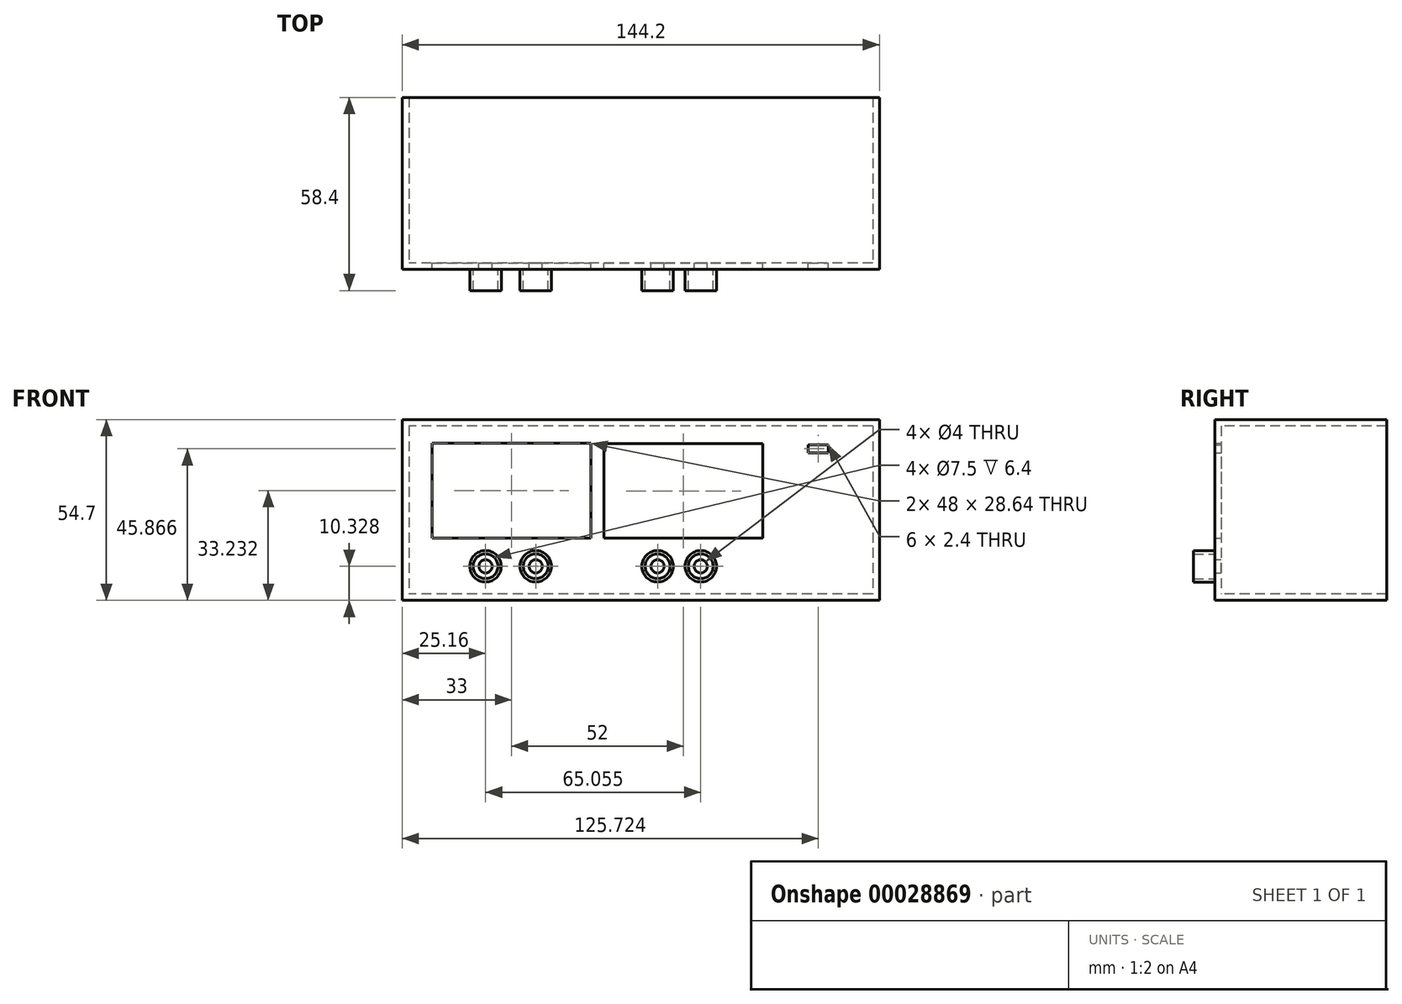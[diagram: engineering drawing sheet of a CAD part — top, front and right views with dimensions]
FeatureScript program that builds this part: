
annotation { "Feature Type Name" : "Feature", "Feature Type Description" : "" }
export const myFeature = defineFeature(function(context is Context, id is Id, definition is map)
    precondition{}
    {
        {
            var Q0;
            Q0=qCreatedBy(makeId("Front.planeOp"),FACE);
            var sketch = newSketch(context, id + "F0", { "sketchPlane" : qUnion([Q0])});
            skLineSegment(sketch, "E0.bottom", {"start": v(0, 54.7) * mm, "end": v(144.2, 54.7) * mm});
            skLineSegment(sketch, "E0.top", {"start": v(0, 0) * mm, "end": v(144.2, 0) * mm});
            skLineSegment(sketch, "E0.left", {"start": v(0, 54.7) * mm, "end": v(0, 0) * mm});
            skLineSegment(sketch, "E0.right", {"start": v(144.2, 54.7) * mm, "end": v(144.2, 0) * mm});
            skLineSegment(sketch, "E1.bottom", {"start": v(9, 47.55) * mm, "end": v(57, 47.55) * mm});
            skLineSegment(sketch, "E1.top", {"start": v(9, 18.91) * mm, "end": v(57, 18.91) * mm});
            skLineSegment(sketch, "E1.left", {"start": v(9, 47.55) * mm, "end": v(9, 18.91) * mm});
            skLineSegment(sketch, "E1.right", {"start": v(57, 47.55) * mm, "end": v(57, 18.91) * mm});
            skLineSegment(sketch, "E2.bottom", {"start": v(61, 47.46) * mm, "end": v(109, 47.46) * mm});
            skLineSegment(sketch, "E2.top", {"start": v(61, 18.82) * mm, "end": v(109, 18.82) * mm});
            skLineSegment(sketch, "E2.left", {"start": v(61, 47.46) * mm, "end": v(61, 18.82) * mm});
            skLineSegment(sketch, "E2.right", {"start": v(109, 47.46) * mm, "end": v(109, 18.82) * mm});
            skLineSegment(sketch, "E3.bottom", {"start": v(122.72, 47.07) * mm, "end": v(128.72, 47.07) * mm});
            skLineSegment(sketch, "E3.top", {"start": v(122.72, 44.67) * mm, "end": v(128.72, 44.67) * mm});
            skLineSegment(sketch, "E3.left", {"start": v(122.72, 47.07) * mm, "end": v(122.72, 44.67) * mm});
            skLineSegment(sketch, "E3.right", {"start": v(128.72, 47.07) * mm, "end": v(128.72, 44.67) * mm});
            skLineSegment(sketch, "E4", {"start": v(0, 10.33) * mm, "end": v(144.2, 10.33) * mm, "construction": true});
            skCircle(sketch, "E5", {"center": v(25.16, 10.33) * mm, "radius": 2 * mm});
            skCircle(sketch, "E6", {"center": v(40.32, 10.33) * mm, "radius": 2 * mm});
            skCircle(sketch, "E7", {"center": v(77.16, 10.33) * mm, "radius": 2 * mm});
            skCircle(sketch, "E8", {"center": v(90.22, 10.33) * mm, "radius": 2 * mm});
            skSolve(sketch);
        }
        {
            var Q0;
            Q0=makeQuery(id+"F0.imprint","IMPRINT",FACE,{"disambiguationData":[TD([[makeQuery(id+"F0.imprint","IMPRINT",EDGE,{"derivedFrom":sQuery(id+"F0.wireOp",EDGE,"E0.bottom")}),-1.0]])]});
            extrude(context, id + "F1", {"entities" : qUnion([Q0]), "depth" : 2 * mm});
        }
        {
            var Q0;
            Q0=makeQuery(id+"F1.opExtrude","CAP_FACE",FACE,{"disambiguationData":[OSD([sQuery(id+"F0.wireOp",EDGE,"E0.bottom"),sQuery(id+"F0.wireOp",EDGE,"E0.top"),sQuery(id+"F0.wireOp",EDGE,"E0.left"),sQuery(id+"F0.wireOp",EDGE,"E0.right"),sQuery(id+"F0.wireOp",EDGE,"E1.bottom"),sQuery(id+"F0.wireOp",EDGE,"E1.top"),sQuery(id+"F0.wireOp",EDGE,"E1.left"),sQuery(id+"F0.wireOp",EDGE,"E1.right"),sQuery(id+"F0.wireOp",EDGE,"E2.bottom"),sQuery(id+"F0.wireOp",EDGE,"E2.top"),sQuery(id+"F0.wireOp",EDGE,"E2.left"),sQuery(id+"F0.wireOp",EDGE,"E2.right"),sQuery(id+"F0.wireOp",EDGE,"E3.bottom"),sQuery(id+"F0.wireOp",EDGE,"E3.top"),sQuery(id+"F0.wireOp",EDGE,"E3.left"),sQuery(id+"F0.wireOp",EDGE,"E3.right"),sQuery(id+"F0.wireOp",EDGE,"E5"),sQuery(id+"F0.wireOp",EDGE,"E6"),sQuery(id+"F0.wireOp",EDGE,"E7"),sQuery(id+"F0.wireOp",EDGE,"E8")])],"isStart":false});
            var sketch = newSketch(context, id + "F2", { "sketchPlane" : qUnion([Q0])});
            skCircle(sketch, "E9", {"center": v(25.16, 10.33) * mm, "radius": 4.75 * mm});
            skCircle(sketch, "E10", {"center": v(40.32, 10.33) * mm, "radius": 4.75 * mm});
            skCircle(sketch, "E11", {"center": v(77.16, 10.33) * mm, "radius": 4.75 * mm});
            skCircle(sketch, "E12", {"center": v(90.22, 10.33) * mm, "radius": 4.75 * mm});
            skCircle(sketch, "E13", {"center": v(25.16, 10.33) * mm, "radius": 3.75 * mm});
            skCircle(sketch, "E14", {"center": v(40.32, 10.33) * mm, "radius": 3.75 * mm});
            skCircle(sketch, "E15", {"center": v(77.16, 10.33) * mm, "radius": 3.75 * mm});
            skCircle(sketch, "E16", {"center": v(90.22, 10.33) * mm, "radius": 3.75 * mm});
            skSolve(sketch);
        }
        {
            var Q0;
            Q0=makeQuery(id+"F2.imprint","IMPRINT",FACE,{"disambiguationData":[TD([[makeQuery(id+"F2.imprint","IMPRINT",EDGE,{"derivedFrom":sQuery(id+"F2.wireOp",EDGE,"E9")}),1.0]])]});
            var Q1;
            Q1=makeQuery(id+"F2.imprint","IMPRINT",FACE,{"disambiguationData":[TD([[makeQuery(id+"F2.imprint","IMPRINT",EDGE,{"derivedFrom":sQuery(id+"F2.wireOp",EDGE,"E10")}),1.0]])]});
            var Q2;
            Q2=makeQuery(id+"F2.imprint","IMPRINT",FACE,{"disambiguationData":[TD([[makeQuery(id+"F2.imprint","IMPRINT",EDGE,{"derivedFrom":sQuery(id+"F2.wireOp",EDGE,"E11")}),1.0]])]});
            var Q3;
            Q3=makeQuery(id+"F2.imprint","IMPRINT",FACE,{"disambiguationData":[TD([[makeQuery(id+"F2.imprint","IMPRINT",EDGE,{"derivedFrom":sQuery(id+"F2.wireOp",EDGE,"E12")}),1.0]])]});
            extrude(context, id + "F3", {"entities" : qUnion([Q0, Q1, Q2, Q3]), "operationType" : NewBodyOperationType.ADD, "depth" : 6.4 * mm});
        }
        {
            var Q0;
            Q0=makeQuery(id+"F1.opExtrude","CAP_FACE",FACE,{"disambiguationData":[OSD([sQuery(id+"F0.wireOp",EDGE,"E0.bottom"),sQuery(id+"F0.wireOp",EDGE,"E0.top"),sQuery(id+"F0.wireOp",EDGE,"E0.left"),sQuery(id+"F0.wireOp",EDGE,"E0.right"),sQuery(id+"F0.wireOp",EDGE,"E1.bottom"),sQuery(id+"F0.wireOp",EDGE,"E1.top"),sQuery(id+"F0.wireOp",EDGE,"E1.left"),sQuery(id+"F0.wireOp",EDGE,"E1.right"),sQuery(id+"F0.wireOp",EDGE,"E2.bottom"),sQuery(id+"F0.wireOp",EDGE,"E2.top"),sQuery(id+"F0.wireOp",EDGE,"E2.left"),sQuery(id+"F0.wireOp",EDGE,"E2.right"),sQuery(id+"F0.wireOp",EDGE,"E3.bottom"),sQuery(id+"F0.wireOp",EDGE,"E3.top"),sQuery(id+"F0.wireOp",EDGE,"E3.left"),sQuery(id+"F0.wireOp",EDGE,"E3.right"),sQuery(id+"F0.wireOp",EDGE,"E5"),sQuery(id+"F0.wireOp",EDGE,"E6"),sQuery(id+"F0.wireOp",EDGE,"E7"),sQuery(id+"F0.wireOp",EDGE,"E8")])],"isStart":true});
            var sketch = newSketch(context, id + "F4", { "sketchPlane" : qUnion([Q0])});
            skLineSegment(sketch, "E17.bottom", {"start": v(-144.2, 54.7) * mm, "end": v(0, 54.7) * mm});
            skLineSegment(sketch, "E17.top", {"start": v(-144.2, 52.7) * mm, "end": v(0, 52.7) * mm});
            skLineSegment(sketch, "E17.left", {"start": v(-144.2, 54.7) * mm, "end": v(-144.2, 52.7) * mm});
            skLineSegment(sketch, "E17.right", {"start": v(0, 54.7) * mm, "end": v(0, 52.7) * mm});
            skLineSegment(sketch, "E18.bottom", {"start": v(-144.2, 2) * mm, "end": v(0, 2) * mm});
            skLineSegment(sketch, "E18.top", {"start": v(-144.2, 0) * mm, "end": v(0, 0) * mm});
            skLineSegment(sketch, "E18.left", {"start": v(-144.2, 2) * mm, "end": v(-144.2, 0) * mm});
            skLineSegment(sketch, "E18.right", {"start": v(0, 2) * mm, "end": v(0, 0) * mm});
            skLineSegment(sketch, "E19.bottom", {"start": v(-144.2, 54.7) * mm, "end": v(-142.2, 54.7) * mm});
            skLineSegment(sketch, "E19.top", {"start": v(-144.2, 0) * mm, "end": v(-142.2, 0) * mm});
            skLineSegment(sketch, "E19.left", {"start": v(-144.2, 54.7) * mm, "end": v(-144.2, 0) * mm});
            skLineSegment(sketch, "E19.right", {"start": v(-142.2, 54.7) * mm, "end": v(-142.2, 0) * mm});
            skLineSegment(sketch, "E20.bottom", {"start": v(-2, 54.7) * mm, "end": v(0, 54.7) * mm});
            skLineSegment(sketch, "E20.top", {"start": v(-2, 0) * mm, "end": v(0, 0) * mm});
            skLineSegment(sketch, "E20.left", {"start": v(-2, 54.7) * mm, "end": v(-2, 0) * mm});
            skLineSegment(sketch, "E20.right", {"start": v(0, 54.7) * mm, "end": v(0, 0) * mm});
            skSolve(sketch);
        }
        {
            var Q0;
            Q0 = qSketchRegion(id + "F4", true);
            extrude(context, id + "F5", {"entities" : qUnion([Q0]), "operationType" : NewBodyOperationType.ADD, "depth" : 50 * mm});
        }
    });
